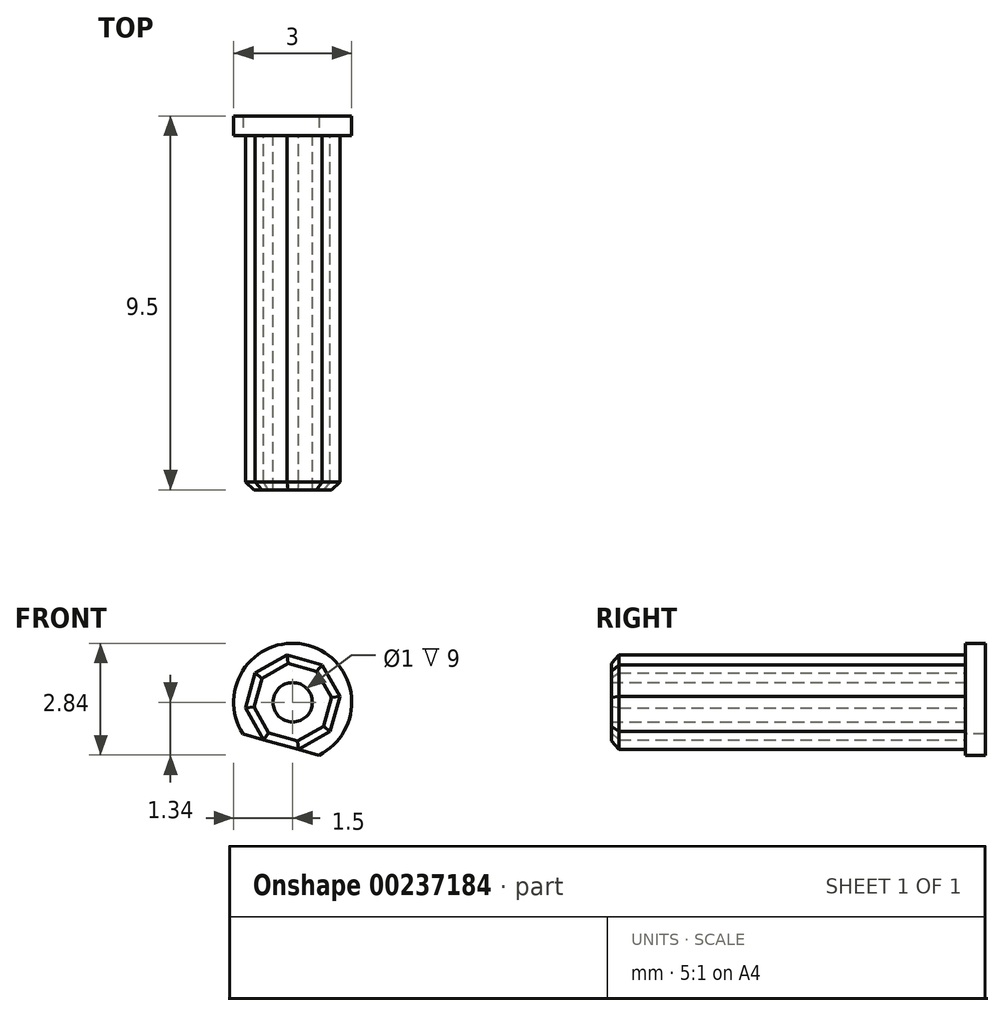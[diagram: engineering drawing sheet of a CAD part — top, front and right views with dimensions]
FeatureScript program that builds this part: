
annotation { "Feature Type Name" : "Feature", "Feature Type Description" : "" }
export const myFeature = defineFeature(function(context is Context, id is Id, definition is map)
    precondition{}
    {
        {
            var Q0;
            Q0=qCreatedBy(makeId("Front.planeOp"),FACE);
            var sketch = newSketch(context, id + "F0", { "sketchPlane" : qUnion([Q0])});
            skCircle(sketch, "E0.cCircle", {"center": v(0, 0) * mm, "radius": 1.2 * mm, "construction": true});
            skLineSegment(sketch, "E0.0", {"start": v(0.75, 0.95) * mm, "end": v(1.2, 0.15) * mm});
            skLineSegment(sketch, "E0.1", {"start": v(1.2, 0.15) * mm, "end": v(0.95, -0.75) * mm});
            skLineSegment(sketch, "E0.2", {"start": v(0.95, -0.75) * mm, "end": v(0.15, -1.2) * mm});
            skLineSegment(sketch, "E0.3", {"start": v(0.15, -1.2) * mm, "end": v(-0.75, -0.95) * mm});
            skLineSegment(sketch, "E0.4", {"start": v(-0.75, -0.95) * mm, "end": v(-1.2, -0.15) * mm});
            skLineSegment(sketch, "E0.5", {"start": v(-1.2, -0.15) * mm, "end": v(-0.95, 0.75) * mm});
            skLineSegment(sketch, "E0.6", {"start": v(-0.95, 0.75) * mm, "end": v(-0.15, 1.2) * mm});
            skLineSegment(sketch, "E0.7", {"start": v(-0.15, 1.2) * mm, "end": v(0.75, 0.95) * mm});
            skCircle(sketch, "E1", {"center": v(0, 0) * mm, "radius": 0.5 * mm});
            skCircle(sketch, "E2", {"center": v(0, 0) * mm, "radius": 1.5 * mm});
            skLineSegment(sketch, "E3", {"start": v(0.15, -1.2) * mm, "end": v(0.66, -1.34) * mm});
            skLineSegment(sketch, "E4", {"start": v(0.66, -1.34) * mm, "end": v(-1.26, -0.8) * mm});
            skSolve(sketch);
        }
        {
            var Q0;
            Q0=makeQuery(id+"F0.imprint","IMPRINT",FACE,{"disambiguationData":[TD([[makeQuery(id+"F0.imprint","IMPRINT",EDGE,{"derivedFrom":sQuery(id+"F0.wireOp",EDGE,"E0.0")}),-1.0]])]});
            extrude(context, id + "F1", {"entities" : qUnion([Q0]), "depth" : 9 * mm});
        }
        {
            var Q0;
            Q0=makeQuery(id+"F1.opExtrude","CAP_EDGE",EDGE,{"disambiguationData":[OSD([sQuery(id+"F0.wireOp",EDGE,"E0.6")])],"isStart":false});
            var Q1;
            Q1=makeQuery(id+"F1.opExtrude","CAP_EDGE",EDGE,{"disambiguationData":[OSD([sQuery(id+"F0.wireOp",EDGE,"E0.5")])],"isStart":false});
            var Q2;
            Q2=makeQuery(id+"F1.opExtrude","CAP_EDGE",EDGE,{"disambiguationData":[OSD([sQuery(id+"F0.wireOp",EDGE,"E0.4")])],"isStart":false});
            var Q3;
            Q3=makeQuery(id+"F1.opExtrude","CAP_EDGE",EDGE,{"disambiguationData":[OSD([sQuery(id+"F0.wireOp",EDGE,"E0.3")])],"isStart":false});
            var Q4;
            Q4=makeQuery(id+"F1.opExtrude","CAP_EDGE",EDGE,{"disambiguationData":[OSD([sQuery(id+"F0.wireOp",EDGE,"E0.2")])],"isStart":false});
            var Q5;
            Q5=makeQuery(id+"F1.opExtrude","CAP_EDGE",EDGE,{"disambiguationData":[OSD([sQuery(id+"F0.wireOp",EDGE,"E0.1")])],"isStart":false});
            var Q6;
            Q6=makeQuery(id+"F1.opExtrude","CAP_EDGE",EDGE,{"disambiguationData":[OSD([sQuery(id+"F0.wireOp",EDGE,"E0.0")])],"isStart":false});
            var Q7;
            Q7=makeQuery(id+"F1.opExtrude","CAP_EDGE",EDGE,{"disambiguationData":[OSD([sQuery(id+"F0.wireOp",EDGE,"E0.7")])],"isStart":false});
            chamfer(context, id + "F2", {"entities" : qUnion([Q0, Q1, Q2, Q3, Q4, Q5, Q6, Q7]), "width" : .2 * mm, "tangentPropagation" : true});
        }
        {
            var Q0;
            Q0=makeQuery(id+"F0.imprint","IMPRINT",FACE,{"disambiguationData":[TD([[makeQuery(id+"F0.imprint","IMPRINT",EDGE,{"derivedFrom":sQuery(id+"F0.wireOp",EDGE,"E0.0")}),1.0]])]});
            var Q1;
            Q1=makeQuery(id+"F0.imprint","IMPRINT",FACE,{"disambiguationData":[TD([[makeQuery(id+"F0.imprint","IMPRINT",EDGE,{"derivedFrom":sQuery(id+"F0.wireOp",EDGE,"E0.0")}),-1.0]])]});
            var Q2;
            Q2=makeQuery(id+"F0.imprint","IMPRINT",FACE,{"disambiguationData":[TD([[makeQuery(id+"F0.imprint","IMPRINT",EDGE,{"derivedFrom":sQuery(id+"F0.wireOp",EDGE,"E1")}),1.0]])]});
            extrude(context, id + "F3", {"entities" : qUnion([Q0, Q1, Q2]), "operationType" : NewBodyOperationType.ADD, "oppositeDirection" : true, "depth" : 0.5 * mm});
        }
    });
